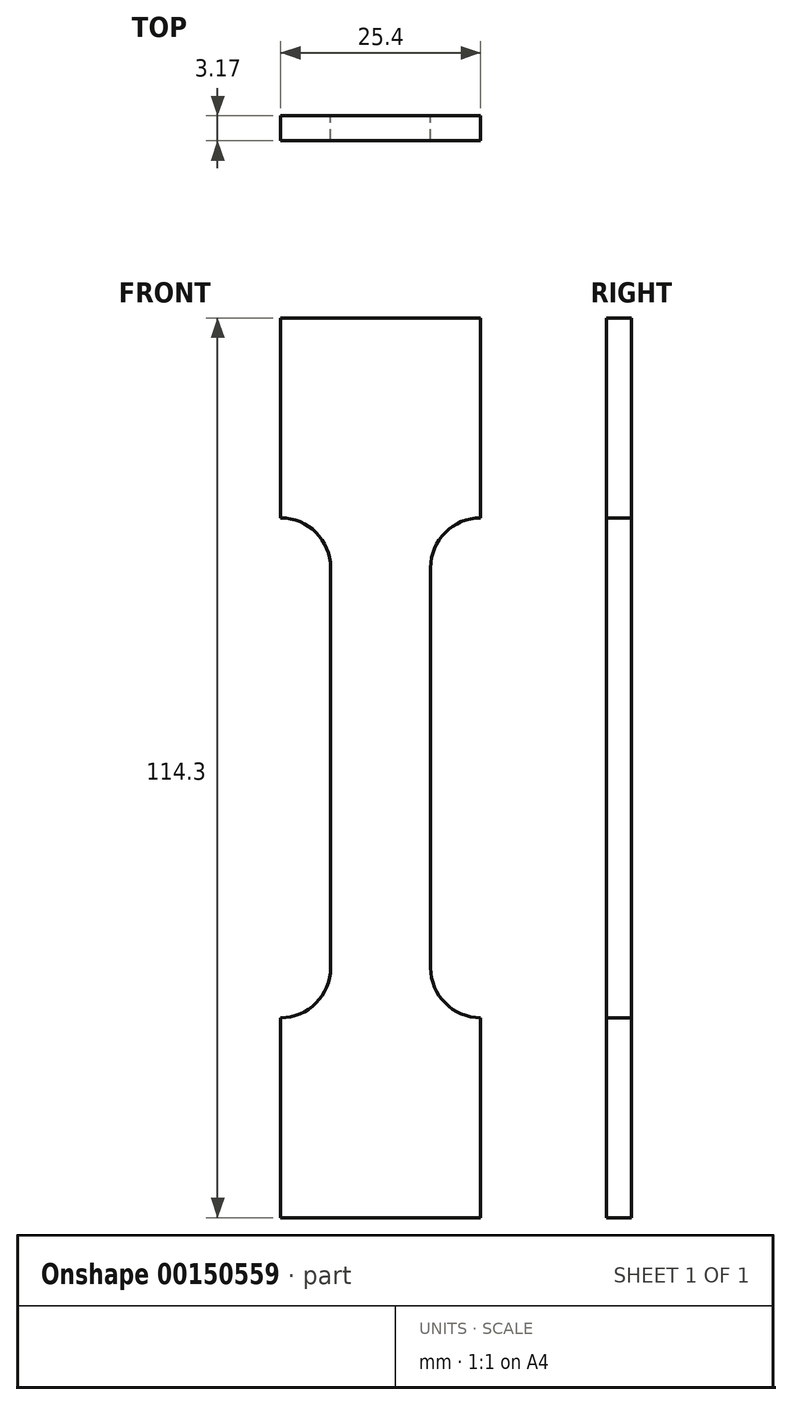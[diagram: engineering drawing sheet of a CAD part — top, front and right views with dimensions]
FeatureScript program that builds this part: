
annotation { "Feature Type Name" : "Feature", "Feature Type Description" : "" }
export const myFeature = defineFeature(function(context is Context, id is Id, definition is map)
    precondition{}
    {
        {
            var Q0;
            Q0=qCreatedBy(makeId("Front.planeOp"),FACE);
            var sketch = newSketch(context, id + "F0", { "sketchPlane" : qUnion([Q0])});
            skLineSegment(sketch, "E0.left", {"start": v(-6.35, -6.35) * mm, "end": v(-6.35, -31.75) * mm});
            skLineSegment(sketch, "E1.bottom", {"start": v(-12.7, 0) * mm, "end": v(-12.7, 0) * mm});
            skLineSegment(sketch, "E1.right", {"start": v(-12.7, 0) * mm, "end": v(-12.7, 25.4) * mm});
            skLineSegment(sketch, "E2", {"start": v(6.35, 0) * mm, "end": v(6.35, 0) * mm});
            skPoint(sketch, "E3.visualSharp", {"position": v(-6.35, 0) * mm});
            skArc(sketch, "E3.filletArc", {"start": v(-6.35, -6.35) * mm, "mid": v(-8.2, -1.86) * mm, "end": v(-12.7, 0) * mm});
            skPoint(sketch, "E4.visualSharp", {"position": v(0, 0) * mm});
            skLineSegment(sketch, "E5", {"start": v(0, 0) * mm, "end": v(-28.44, 0) * mm, "construction": true});
            skLineSegment(sketch, "E6", {"start": v(0, 25.4) * mm, "end": v(0, -31.75) * mm, "construction": true});
            skLineSegment(sketch, "E7", {"start": v(0, 25.4) * mm, "end": v(-12.7, 25.4) * mm});
            skLineSegment(sketch, "E8", {"start": v(-43.84, -31.75) * mm, "end": v(14.75, -31.75) * mm, "construction": true});
            skLineSegment(sketch, "E9.MirrorCS", {"start": v(0, 25.4) * mm, "end": v(12.7, 25.4) * mm});
            skLineSegment(sketch, "E10.MirrorCS", {"start": v(6.35, -6.35) * mm, "end": v(6.35, -31.75) * mm});
            skLineSegment(sketch, "E11.MirrorCS", {"start": v(12.7, 0) * mm, "end": v(12.7, 25.4) * mm});
            skArc(sketch, "E12.MirrorCS", {"start": v(6.35, -6.35) * mm, "mid": v(8.2, -1.86) * mm, "end": v(12.7, 0) * mm});
            skLineSegment(sketch, "E13.MirrorCS", {"start": v(6.35, -57.15) * mm, "end": v(6.35, -31.75) * mm});
            skArc(sketch, "E14.MirrorCS", {"start": v(6.35, -57.15) * mm, "mid": v(8.2, -61.64) * mm, "end": v(12.7, -63.5) * mm});
            skLineSegment(sketch, "E15.MirrorCS", {"start": v(12.7, -63.5) * mm, "end": v(12.7, -88.9) * mm});
            skLineSegment(sketch, "E16.MirrorCS", {"start": v(0, -88.9) * mm, "end": v(12.7, -88.9) * mm});
            skLineSegment(sketch, "E17.MirrorCS", {"start": v(0, -88.9) * mm, "end": v(-12.7, -88.9) * mm});
            skLineSegment(sketch, "E18.MirrorCS", {"start": v(-6.35, -57.15) * mm, "end": v(-6.35, -31.75) * mm});
            skLineSegment(sketch, "E19.MirrorCS", {"start": v(-12.7, -63.5) * mm, "end": v(-12.7, -88.9) * mm});
            skArc(sketch, "E20.MirrorCS", {"start": v(-6.35, -57.15) * mm, "mid": v(-8.2, -61.64) * mm, "end": v(-12.7, -63.5) * mm});
            skSolve(sketch);
        }
        {
            var Q0;
            Q0=makeQuery(id+"F0.imprint","IMPRINT",FACE,{"disambiguationData":[TD([[makeQuery(id+"F0.imprint","IMPRINT",EDGE,{"derivedFrom":sQuery(id+"F0.wireOp",EDGE,"E0.left")}),1.0]])]});
            extrude(context, id + "F1", {"entities" : qUnion([Q0]), "depth" : 3.17 * mm});
        }
    });
